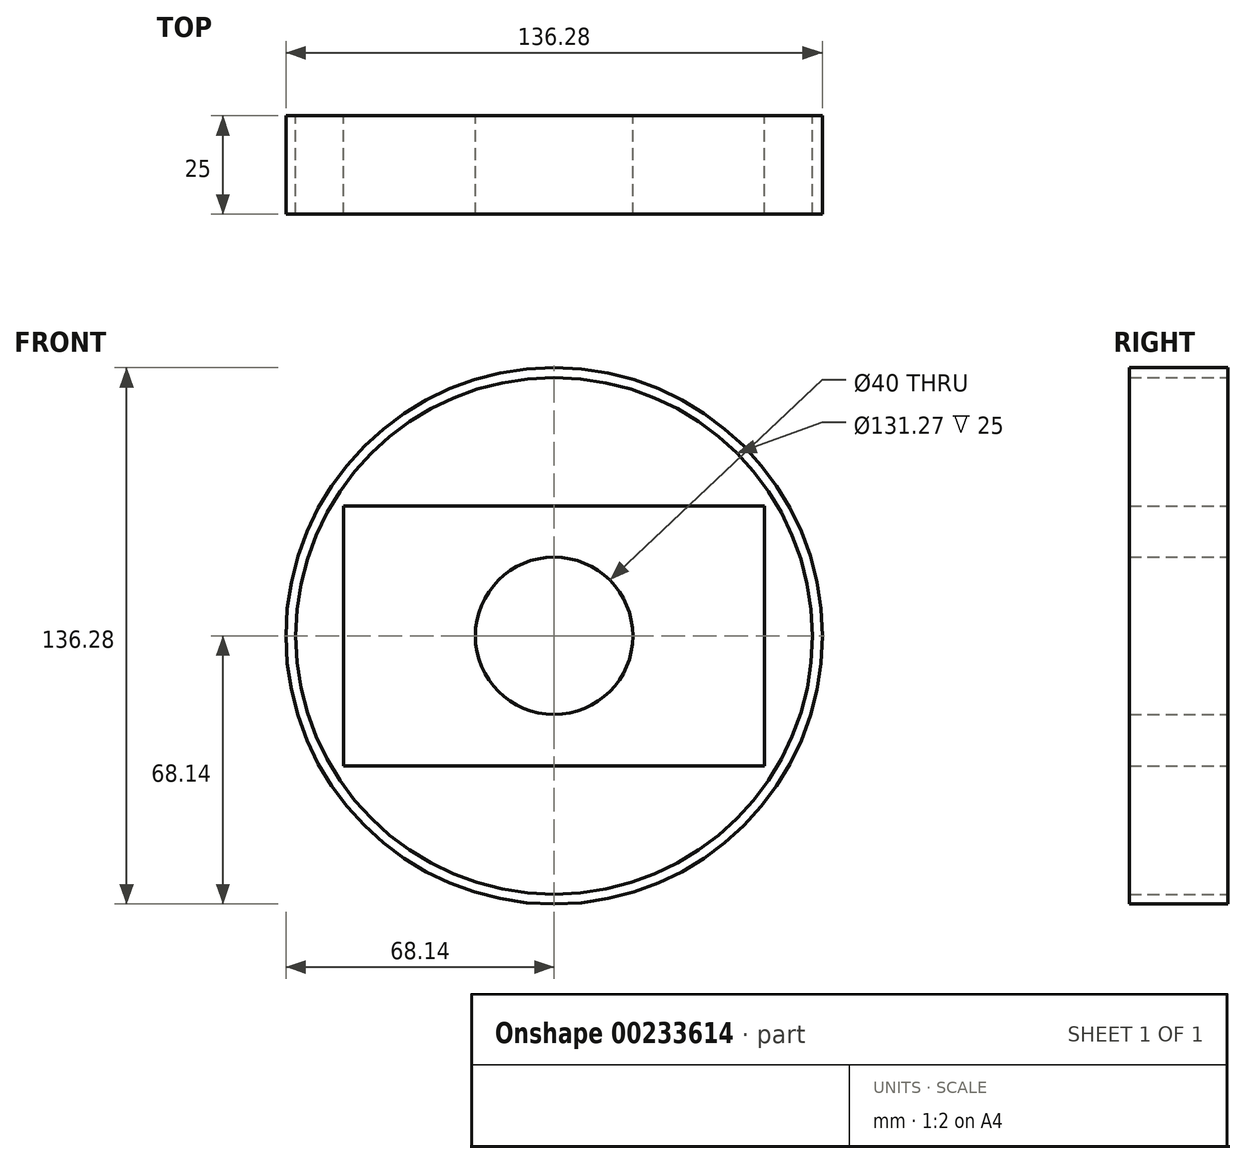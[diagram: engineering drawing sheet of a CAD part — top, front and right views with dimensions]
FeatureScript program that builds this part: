
annotation { "Feature Type Name" : "Feature", "Feature Type Description" : "" }
export const myFeature = defineFeature(function(context is Context, id is Id, definition is map)
    precondition{}
    {
        {
            var Q0;
            Q0=qCreatedBy(makeId("Front.planeOp"),FACE);
            var sketch = newSketch(context, id + "F0", { "sketchPlane" : qUnion([Q0])});
            skCircle(sketch, "E0", {"center": v(0, 0) * mm, "radius": 68.14 * mm});
            skSolve(sketch);
        }
        {
            var Q0;
            Q0=makeQuery(id+"F0.imprint","IMPRINT",FACE,{"disambiguationData":[TD([[makeQuery(id+"F0.imprint","IMPRINT",EDGE,{"derivedFrom":sQuery(id+"F0.wireOp",EDGE,"E0")}),1.0]])]});
            extrude(context, id + "F1", {"entities" : qUnion([Q0]), "depth" : 25 * mm});
        }
        {
            var Q0;
            Q0=makeQuery(id+"F1.opExtrude","CAP_FACE",FACE,{"disambiguationData":[OSD([sQuery(id+"F0.wireOp",EDGE,"E0")])],"isStart":false});
            var Q1;
            Q1=makeQuery(id+"F1.opExtrude","CAP_FACE",FACE,{"disambiguationData":[OSD([sQuery(id+"F0.wireOp",EDGE,"E0")])],"isStart":true});
            shell(context, id + "F2", {"entities" : qUnion([Q0, Q1]), "thickness" : 2.5 * mm});
        }
        {
            var Q0;
            Q0=qCreatedBy(makeId("Front.planeOp"),FACE);
            var sketch = newSketch(context, id + "F3", { "sketchPlane" : qUnion([Q0])});
            skLineSegment(sketch, "E1.bottom", {"start": v(-53.5, 33) * mm, "end": v(53.5, 33) * mm});
            skLineSegment(sketch, "E1.top", {"start": v(-53.5, -33) * mm, "end": v(53.5, -33) * mm});
            skLineSegment(sketch, "E1.left", {"start": v(-53.5, 33) * mm, "end": v(-53.5, -33) * mm});
            skLineSegment(sketch, "E1.right", {"start": v(53.5, 33) * mm, "end": v(53.5, -33) * mm});
            skPoint(sketch, "E1.middle", {"position": v(0, 0) * mm});
            skSolve(sketch);
        }
        {
            var Q0;
            Q0=makeQuery(id+"F3.imprint","IMPRINT",FACE,{"disambiguationData":[TD([[makeQuery(id+"F3.imprint","IMPRINT",EDGE,{"derivedFrom":sQuery(id+"F3.wireOp",EDGE,"E1.bottom")}),-1.0]])]});
            extrude(context, id + "F4", {"entities" : qUnion([Q0]), "depth" : 25 * mm});
        }
        {
            var Q0;
            Q0=qCreatedBy(makeId("Front.planeOp"),FACE);
            var sketch = newSketch(context, id + "F5", { "sketchPlane" : qUnion([Q0])});
            skPoint(sketch, "E2", {"position": v(0, 18.01) * mm});
            skPoint(sketch, "E3", {"position": v(18.67, 0) * mm});
            skPoint(sketch, "E4", {"position": v(0, -15.9) * mm});
            skPoint(sketch, "E5", {"position": v(-17.1, 0) * mm});
            skArc(sketch, "E6", {"start": v(-18.14, 6.18) * mm, "mid": v(18.9, -3.13) * mm, "end": v(-19.17, 0) * mm});
            skSolve(sketch);
        }
        {
            var Q0;
            Q0=sQuery(id+"F5.wireOp",VERTEX,"E6.center");
            var Q1;
            Q1=makeQuery(id+"F4.opExtrude","SWEPT_BODY",BODY,{"disambiguationData":[OSD([sQuery(id+"F3.wireOp",EDGE,"E1.bottom"),sQuery(id+"F3.wireOp",EDGE,"E1.top"),sQuery(id+"F3.wireOp",EDGE,"E1.left"),sQuery(id+"F3.wireOp",EDGE,"E1.right")])]});
            hole(context, id + "F6", {"style" : HoleStyle.SIMPLE, "endStyle" : HoleEndStyle.THROUGH, "oppositeDirection" : true, "holeDiameter" : 40 * mm, "locations" : qUnion([Q0]), "scope" : qUnion([Q1]), "isTappedThrough" : true});
        }
    });
